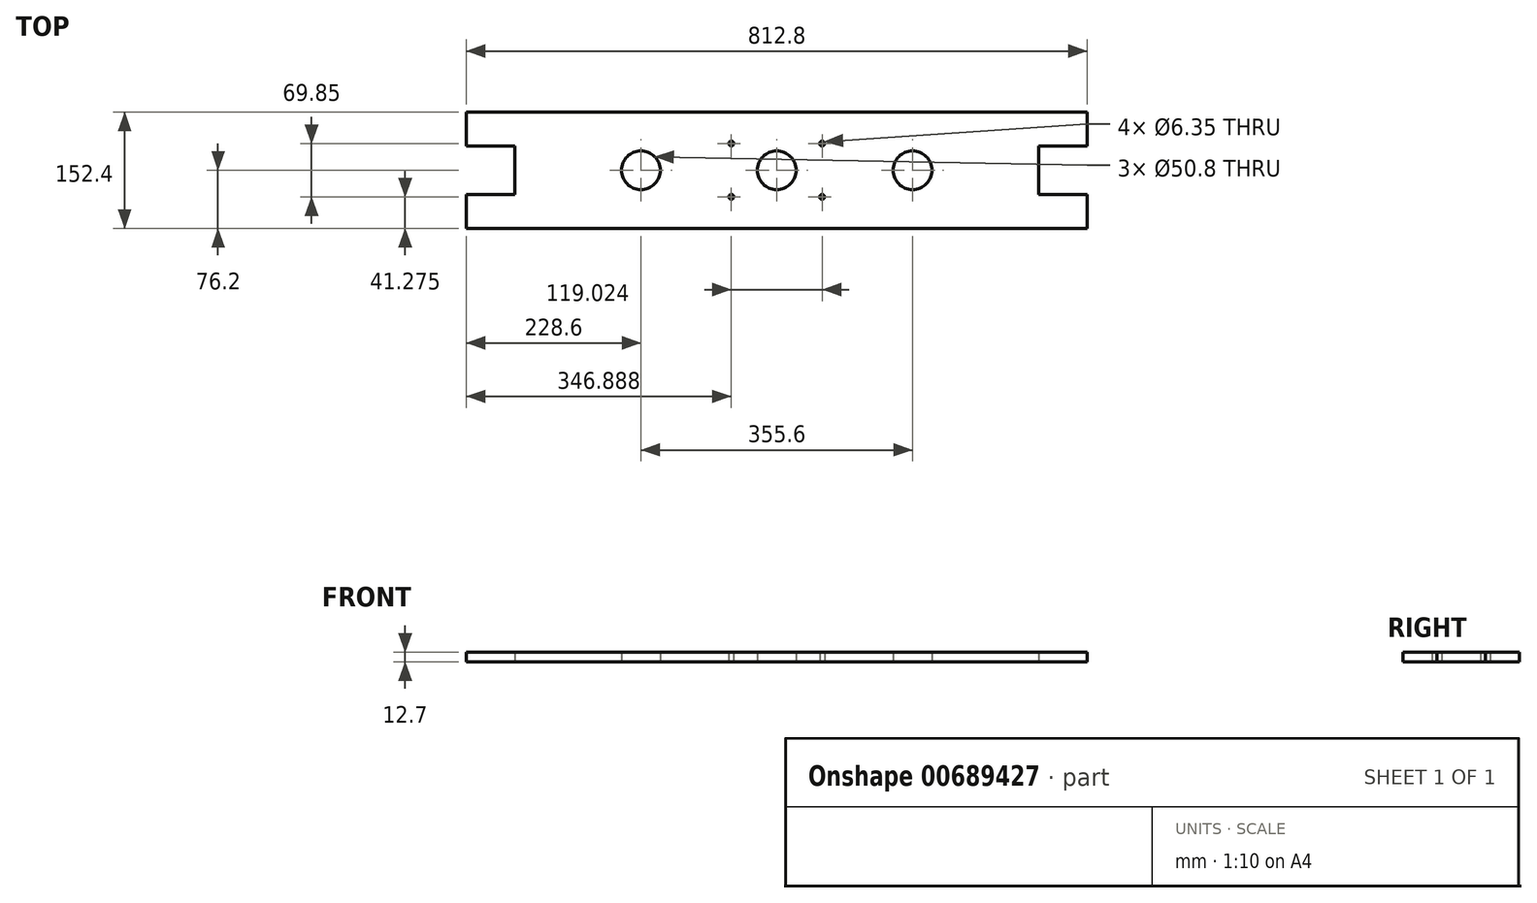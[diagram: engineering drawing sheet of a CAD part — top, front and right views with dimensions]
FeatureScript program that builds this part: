
annotation { "Feature Type Name" : "Feature", "Feature Type Description" : "" }
export const myFeature = defineFeature(function(context is Context, id is Id, definition is map)
    precondition{}
    {
        {
            var Q0;
            Q0=qCreatedBy(makeId("Top.planeOp"),FACE);
            var sketch = newSketch(context, id + "F0", { "sketchPlane" : qUnion([Q0])});
            skLineSegment(sketch, "E0.bottom", {"start": v(-406.4, 76.2) * mm, "end": v(406.4, 76.2) * mm});
            skLineSegment(sketch, "E0.top", {"start": v(-406.4, -76.2) * mm, "end": v(406.4, -76.2) * mm});
            skLineSegment(sketch, "E0.left", {"start": v(-406.4, 76.2) * mm, "end": v(-406.4, 31.75) * mm});
            skLineSegment(sketch, "E0.right", {"start": v(406.4, 76.2) * mm, "end": v(406.4, 31.75) * mm});
            skPoint(sketch, "E0.middle", {"position": v(374.65, 0) * mm});
            skLineSegment(sketch, "E1.bottom", {"start": v(342.9, 31.75) * mm, "end": v(406.4, 31.75) * mm});
            skLineSegment(sketch, "E1.top", {"start": v(342.9, -31.75) * mm, "end": v(406.4, -31.75) * mm});
            skLineSegment(sketch, "E1.left", {"start": v(342.9, 31.75) * mm, "end": v(342.9, -31.75) * mm});
            skLineSegment(sketch, "E1.right", {"start": v(406.4, 31.75) * mm, "end": v(406.4, 31.75) * mm});
            skLineSegment(sketch, "E2.bottom", {"start": v(-406.4, 31.75) * mm, "end": v(-342.9, 31.75) * mm});
            skLineSegment(sketch, "E2.top", {"start": v(-406.4, -31.75) * mm, "end": v(-342.9, -31.75) * mm});
            skLineSegment(sketch, "E2.left", {"start": v(-406.4, 31.75) * mm, "end": v(-406.4, 31.75) * mm});
            skLineSegment(sketch, "E2.right", {"start": v(-342.9, 31.75) * mm, "end": v(-342.9, -31.75) * mm});
            skPoint(sketch, "E2.middle", {"position": v(-374.65, 0) * mm});
            skLineSegment(sketch, "E3", {"start": v(-406.4, -31.75) * mm, "end": v(-406.4, -31.75) * mm});
            skLineSegment(sketch, "E4", {"start": v(-406.4, -31.75) * mm, "end": v(-406.4, -76.2) * mm});
            skLineSegment(sketch, "E5", {"start": v(406.4, -31.75) * mm, "end": v(406.4, -76.2) * mm});
            skLineSegment(sketch, "E6", {"start": v(406.4, -31.75) * mm, "end": v(406.4, -31.75) * mm});
            skCircle(sketch, "E7", {"center": v(-177.8, 0) * mm, "radius": 25.4 * mm});
            skCircle(sketch, "E8", {"center": v(177.8, 0) * mm, "radius": 25.4 * mm});
            skCircle(sketch, "E9", {"center": v(0, 0) * mm, "radius": 25.4 * mm});
            skCircle(sketch, "E10", {"center": v(-59.51, 34.93) * mm, "radius": 3.18 * mm});
            skCircle(sketch, "E11", {"center": v(59.51, 34.93) * mm, "radius": 3.18 * mm});
            skCircle(sketch, "E12", {"center": v(59.51, -34.93) * mm, "radius": 3.18 * mm});
            skCircle(sketch, "E13", {"center": v(-59.51, -34.93) * mm, "radius": 3.18 * mm});
            skSolve(sketch);
        }
        {
            var Q0;
            Q0=makeQuery(id+"F0.imprint","IMPRINT",FACE,{"disambiguationData":[TD([[makeQuery(id+"F0.imprint","IMPRINT",EDGE,{"derivedFrom":sQuery(id+"F0.wireOp",EDGE,"E0.bottom")}),-1.0]])]});
            extrude(context, id + "F1", {"entities" : qUnion([Q0]), "depth" : 12.7 * mm, "offsetDistance" : 25.4 * mm});
        }
    });
